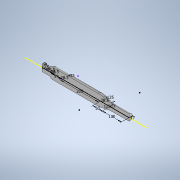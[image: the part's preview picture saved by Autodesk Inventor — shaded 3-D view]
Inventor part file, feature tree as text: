
AUTODESK INVENTOR PART (.ipt)
format: ipt  version: 2022 (Build 260153000, 153)  size: 213,504 bytes
history: native  units: mm
features: sketch x1, revolve x1, extrude x1, fillet x1
ambient origin geometry x8: Origin, YZ Plane, XZ Plane, XY Plane, X Axis, Y Axis, Z Axis, Center Point
bodies: Body1 (feature_tree)
feature tree (4):
  sketch  "Sketch1"  dims[d0=41.0mm d1=6.0mm d2=59.0mm d3=200.0mm d4=50.0mm d5=100.0mm d6=19.5mm d7=19.5mm d8=28.5mm d10=28.5mm d11=17.0mm d12=17.0mm d13=2.0mm d14=8.0mm d16=125.0mm d17=125.0mm d18=2.0mm d25=35.0mm d26=28.5mm d27=180.0deg d28=100.0mm d29=0.0mm d30=2.0mm d19=0.872665mm d20=0.872665mm d31=0.0mm d32=0.0mm d33=0.0mm]
  revolve  "Revolution2"  [1 undecoded]
  extrude  "Extrusion2"  Depth=59.0mm
  fillet  "Fillet1"  Radius=200.0mm
note: 1 required parameter value undecoded (feature->parameter linkage not recoverable at this tier; creation-order binding heuristic only, values carry confidence <= 0.55)
